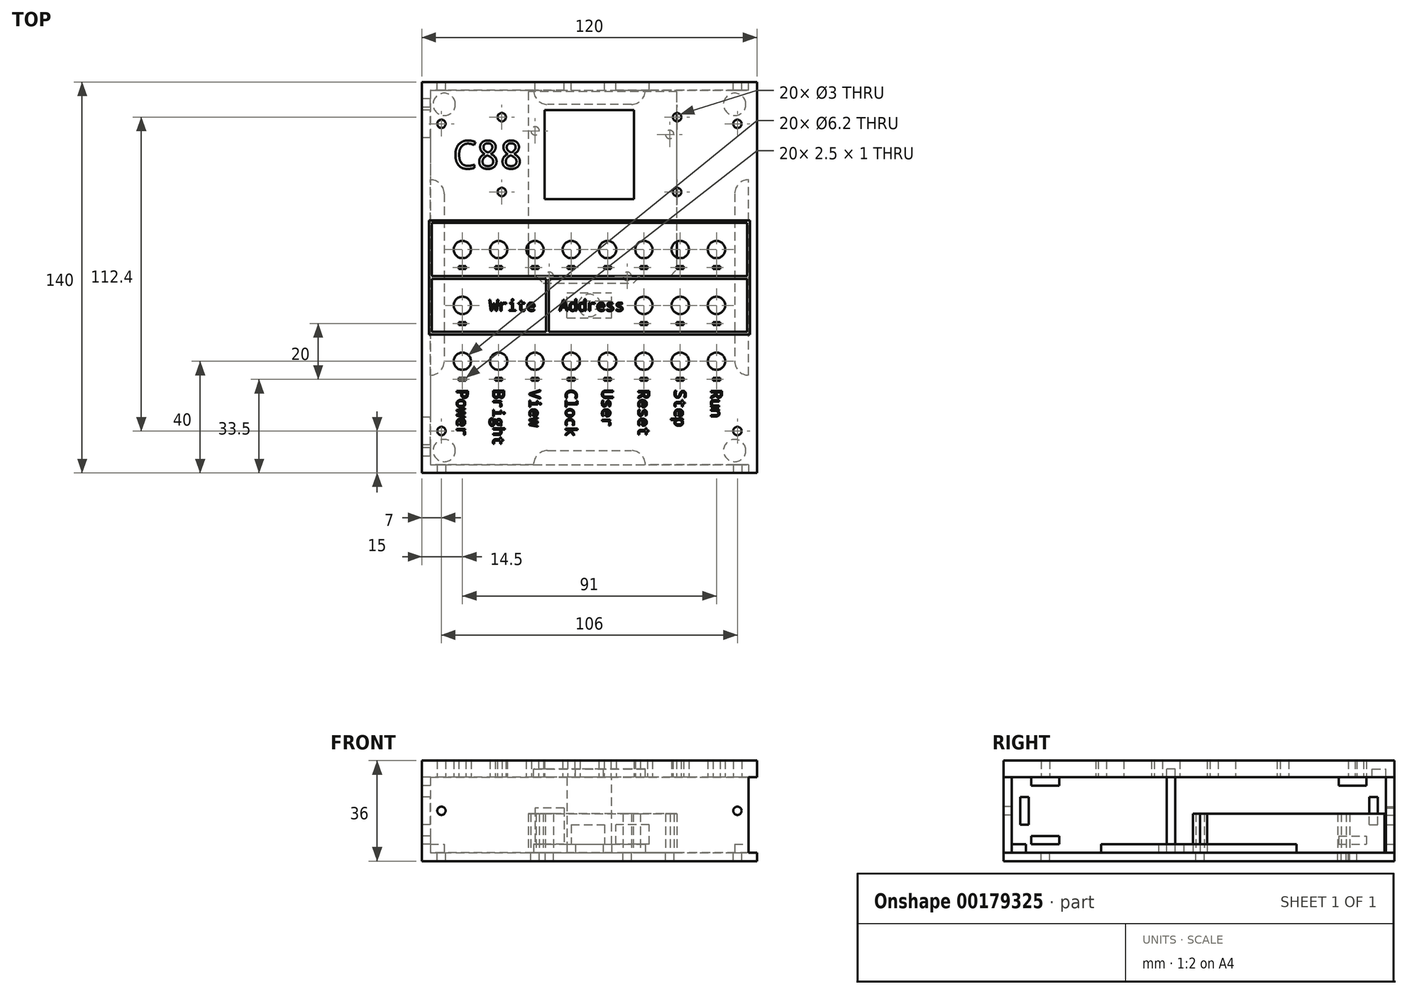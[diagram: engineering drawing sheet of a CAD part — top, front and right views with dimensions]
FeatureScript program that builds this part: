
annotation { "Feature Type Name" : "Feature", "Feature Type Description" : "" }
export const myFeature = defineFeature(function(context is Context, id is Id, definition is map)
    precondition{}
    {
        {
            assignVariable(context, id + "F0", {"name" : "thickness", "anyValue" : 3 * mm});
        }
        {
            var Q0;
            Q0=qCreatedBy(makeId("Top.planeOp"),FACE);
            var sketch = newSketch(context, id + "F1", { "sketchPlane" : qUnion([Q0])});
            skLineSegment(sketch, "E0.bottom", {"start": v(16, -16) * mm, "end": v(-16, -16) * mm});
            skLineSegment(sketch, "E0.top", {"start": v(16, 16) * mm, "end": v(-16, 16) * mm});
            skLineSegment(sketch, "E0.left", {"start": v(16, -16) * mm, "end": v(16, 16) * mm});
            skLineSegment(sketch, "E0.right", {"start": v(-16, -16) * mm, "end": v(-16, 16) * mm});
            skPoint(sketch, "E0.middle", {"position": v(0, 0) * mm});
            skCircle(sketch, "E1", {"center": v(31.4, 13.4) * mm, "radius": 1.5 * mm});
            skCircle(sketch, "E2", {"center": v(31.4, -13.4) * mm, "radius": 1.5 * mm});
            skLineSegment(sketch, "E3", {"start": v(-70.64, 0) * mm, "end": v(73.55, 0) * mm, "construction": true});
            skLineSegment(sketch, "E4.bottom", {"start": v(-60, 26) * mm, "end": v(60, 26) * mm});
            skLineSegment(sketch, "E4.top", {"start": v(-60, -114) * mm, "end": v(60, -114) * mm});
            skLineSegment(sketch, "E4.left", {"start": v(-60, 26) * mm, "end": v(-60, -114) * mm});
            skLineSegment(sketch, "E4.right", {"start": v(60, 26) * mm, "end": v(60, -114) * mm});
            skCircle(sketch, "E5", {"center": v(-31.4, -13.4) * mm, "radius": 1.5 * mm});
            skCircle(sketch, "E6", {"center": v(-31.4, 13.4) * mm, "radius": 1.5 * mm});
            skLineSegment(sketch, "E7", {"start": v(0, 36.27) * mm, "end": v(0, -161.9) * mm, "construction": true});
            skCircle(sketch, "E8", {"center": v(-45.5, -34) * mm, "radius": 3.1 * mm});
            skLineSegment(sketch, "E9.bottom", {"start": v(-44.25, -41) * mm, "end": v(-46.75, -41) * mm});
            skLineSegment(sketch, "E9.top", {"start": v(-44.25, -40) * mm, "end": v(-46.75, -40) * mm});
            skLineSegment(sketch, "E9.left", {"start": v(-44.25, -41) * mm, "end": v(-44.25, -40) * mm});
            skLineSegment(sketch, "E9.right", {"start": v(-46.75, -41) * mm, "end": v(-46.75, -40) * mm});
            skPoint(sketch, "E9.middle", {"position": v(-45.5, -40.5) * mm});
            skCircle(sketch, "E10.1.0.0", {"center": v(-32.5, -34) * mm, "radius": 3.1 * mm});
            skPoint(sketch, "E10.1.0.1", {"position": v(-32.5, -40.5) * mm});
            skLineSegment(sketch, "E10.1.0.2", {"start": v(-31.25, -41) * mm, "end": v(-31.25, -40) * mm});
            skLineSegment(sketch, "E10.1.0.3", {"start": v(-31.25, -41) * mm, "end": v(-33.75, -41) * mm});
            skLineSegment(sketch, "E10.1.0.4", {"start": v(-33.75, -41) * mm, "end": v(-33.75, -40) * mm});
            skLineSegment(sketch, "E10.1.0.5", {"start": v(-31.25, -40) * mm, "end": v(-33.75, -40) * mm});
            skCircle(sketch, "E10.2.0.0", {"center": v(-19.5, -34) * mm, "radius": 3.1 * mm});
            skPoint(sketch, "E10.2.0.1", {"position": v(-19.5, -40.5) * mm});
            skLineSegment(sketch, "E10.2.0.2", {"start": v(-18.25, -41) * mm, "end": v(-18.25, -40) * mm});
            skLineSegment(sketch, "E10.2.0.3", {"start": v(-18.25, -41) * mm, "end": v(-20.75, -41) * mm});
            skLineSegment(sketch, "E10.2.0.4", {"start": v(-20.75, -41) * mm, "end": v(-20.75, -40) * mm});
            skLineSegment(sketch, "E10.2.0.5", {"start": v(-18.25, -40) * mm, "end": v(-20.75, -40) * mm});
            skCircle(sketch, "E10.3.0.0", {"center": v(-6.5, -34) * mm, "radius": 3.1 * mm});
            skPoint(sketch, "E10.3.0.1", {"position": v(-6.5, -40.5) * mm});
            skLineSegment(sketch, "E10.3.0.2", {"start": v(-5.25, -41) * mm, "end": v(-5.25, -40) * mm});
            skLineSegment(sketch, "E10.3.0.3", {"start": v(-5.25, -41) * mm, "end": v(-7.75, -41) * mm});
            skLineSegment(sketch, "E10.3.0.4", {"start": v(-7.75, -41) * mm, "end": v(-7.75, -40) * mm});
            skLineSegment(sketch, "E10.3.0.5", {"start": v(-5.25, -40) * mm, "end": v(-7.75, -40) * mm});
            skCircle(sketch, "E10.4.0.0", {"center": v(6.5, -34) * mm, "radius": 3.1 * mm});
            skPoint(sketch, "E10.4.0.1", {"position": v(6.5, -40.5) * mm});
            skLineSegment(sketch, "E10.4.0.2", {"start": v(7.75, -41) * mm, "end": v(7.75, -40) * mm});
            skLineSegment(sketch, "E10.4.0.3", {"start": v(7.75, -41) * mm, "end": v(5.25, -41) * mm});
            skLineSegment(sketch, "E10.4.0.4", {"start": v(5.25, -41) * mm, "end": v(5.25, -40) * mm});
            skLineSegment(sketch, "E10.4.0.5", {"start": v(7.75, -40) * mm, "end": v(5.25, -40) * mm});
            skCircle(sketch, "E10.5.0.0", {"center": v(19.5, -34) * mm, "radius": 3.1 * mm});
            skPoint(sketch, "E10.5.0.1", {"position": v(19.5, -40.5) * mm});
            skLineSegment(sketch, "E10.5.0.2", {"start": v(20.75, -41) * mm, "end": v(20.75, -40) * mm});
            skLineSegment(sketch, "E10.5.0.3", {"start": v(20.75, -41) * mm, "end": v(18.25, -41) * mm});
            skLineSegment(sketch, "E10.5.0.4", {"start": v(18.25, -41) * mm, "end": v(18.25, -40) * mm});
            skLineSegment(sketch, "E10.5.0.5", {"start": v(20.75, -40) * mm, "end": v(18.25, -40) * mm});
            skCircle(sketch, "E10.6.0.0", {"center": v(32.5, -34) * mm, "radius": 3.1 * mm});
            skPoint(sketch, "E10.6.0.1", {"position": v(32.5, -40.5) * mm});
            skLineSegment(sketch, "E10.6.0.2", {"start": v(33.75, -41) * mm, "end": v(33.75, -40) * mm});
            skLineSegment(sketch, "E10.6.0.3", {"start": v(33.75, -41) * mm, "end": v(31.25, -41) * mm});
            skLineSegment(sketch, "E10.6.0.4", {"start": v(31.25, -41) * mm, "end": v(31.25, -40) * mm});
            skLineSegment(sketch, "E10.6.0.5", {"start": v(33.75, -40) * mm, "end": v(31.25, -40) * mm});
            skCircle(sketch, "E10.7.0.0", {"center": v(45.5, -34) * mm, "radius": 3.1 * mm});
            skPoint(sketch, "E10.7.0.1", {"position": v(45.5, -40.5) * mm});
            skLineSegment(sketch, "E10.7.0.2", {"start": v(46.75, -41) * mm, "end": v(46.75, -40) * mm});
            skLineSegment(sketch, "E10.7.0.3", {"start": v(46.75, -41) * mm, "end": v(44.25, -41) * mm});
            skLineSegment(sketch, "E10.7.0.4", {"start": v(44.25, -41) * mm, "end": v(44.25, -40) * mm});
            skLineSegment(sketch, "E10.7.0.5", {"start": v(46.75, -40) * mm, "end": v(44.25, -40) * mm});
            skLineSegment(sketch, "E10.direction1", {"start": v(-46.75, -41) * mm, "end": v(-33.75, -41) * mm, "construction": true});
            skCircle(sketch, "E11.1.0.0", {"center": v(32.5, -54) * mm, "radius": 3.1 * mm});
            skPoint(sketch, "E11.1.0.1", {"position": v(32.5, -60.5) * mm});
            skPoint(sketch, "E11.1.0.2", {"position": v(19.5, -60.5) * mm});
            skCircle(sketch, "E11.1.0.3", {"center": v(45.5, -54) * mm, "radius": 3.1 * mm});
            skCircle(sketch, "E11.1.0.4", {"center": v(19.5, -54) * mm, "radius": 3.1 * mm});
            skPoint(sketch, "E11.1.0.5", {"position": v(45.5, -60.5) * mm});
            skLineSegment(sketch, "E11.1.0.6", {"start": v(33.75, -61) * mm, "end": v(31.25, -61) * mm});
            skLineSegment(sketch, "E11.1.0.7", {"start": v(46.75, -60) * mm, "end": v(44.25, -60) * mm});
            skLineSegment(sketch, "E11.1.0.8", {"start": v(46.75, -61) * mm, "end": v(46.75, -60) * mm});
            skLineSegment(sketch, "E11.1.0.9", {"start": v(20.75, -61) * mm, "end": v(18.25, -61) * mm});
            skLineSegment(sketch, "E11.1.0.10", {"start": v(33.75, -60) * mm, "end": v(31.25, -60) * mm});
            skLineSegment(sketch, "E11.1.0.11", {"start": v(44.25, -61) * mm, "end": v(44.25, -60) * mm});
            skLineSegment(sketch, "E11.1.0.12", {"start": v(20.75, -60) * mm, "end": v(18.25, -60) * mm});
            skLineSegment(sketch, "E11.1.0.13", {"start": v(46.75, -61) * mm, "end": v(44.25, -61) * mm});
            skLineSegment(sketch, "E11.1.0.14", {"start": v(31.25, -61) * mm, "end": v(31.25, -60) * mm});
            skLineSegment(sketch, "E11.1.0.15", {"start": v(20.75, -61) * mm, "end": v(20.75, -60) * mm});
            skLineSegment(sketch, "E11.1.0.16", {"start": v(33.75, -61) * mm, "end": v(33.75, -60) * mm});
            skLineSegment(sketch, "E11.1.0.17", {"start": v(18.25, -61) * mm, "end": v(18.25, -60) * mm});
            skLineSegment(sketch, "E11.direction1", {"start": v(18.25, -41) * mm, "end": v(18.25, -61) * mm, "construction": true});
            skPoint(sketch, "E12.1.0.0", {"position": v(-45.5, -60.5) * mm});
            skCircle(sketch, "E12.1.0.1", {"center": v(-45.5, -54) * mm, "radius": 3.1 * mm});
            skLineSegment(sketch, "E12.1.0.2", {"start": v(-44.25, -61) * mm, "end": v(-46.75, -61) * mm});
            skLineSegment(sketch, "E12.1.0.3", {"start": v(-44.25, -60) * mm, "end": v(-46.75, -60) * mm});
            skLineSegment(sketch, "E12.1.0.4", {"start": v(-44.25, -61) * mm, "end": v(-44.25, -60) * mm});
            skLineSegment(sketch, "E12.1.0.5", {"start": v(-46.75, -61) * mm, "end": v(-46.75, -60) * mm});
            skLineSegment(sketch, "E12.direction1", {"start": v(-46.75, -41) * mm, "end": v(-46.75, -61) * mm, "construction": true});
            skPoint(sketch, "E13.0.2.0", {"position": v(-45.5, -80.5) * mm});
            skCircle(sketch, "E13.1.2.0", {"center": v(-45.5, -74) * mm, "radius": 3.1 * mm});
            skLineSegment(sketch, "E13.3.2.0", {"start": v(-44.25, -81) * mm, "end": v(-46.75, -81) * mm});
            skLineSegment(sketch, "E13.6.2.0", {"start": v(-44.25, -80) * mm, "end": v(-46.75, -80) * mm});
            skLineSegment(sketch, "E13.9.2.0", {"start": v(-44.25, -81) * mm, "end": v(-44.25, -80) * mm});
            skLineSegment(sketch, "E13.12.2.0", {"start": v(-46.75, -81) * mm, "end": v(-46.75, -80) * mm});
            skLineSegment(sketch, "E14.1.0.0", {"start": v(-31.25, -80) * mm, "end": v(-33.75, -80) * mm});
            skLineSegment(sketch, "E14.1.0.1", {"start": v(-31.25, -81) * mm, "end": v(-33.75, -81) * mm});
            skLineSegment(sketch, "E14.1.0.2", {"start": v(-31.25, -81) * mm, "end": v(-31.25, -80) * mm});
            skLineSegment(sketch, "E14.1.0.3", {"start": v(-33.75, -81) * mm, "end": v(-33.75, -80) * mm});
            skPoint(sketch, "E14.1.0.4", {"position": v(-32.5, -80.5) * mm});
            skCircle(sketch, "E14.1.0.5", {"center": v(-32.5, -74) * mm, "radius": 3.1 * mm});
            skLineSegment(sketch, "E14.2.0.0", {"start": v(-18.25, -80) * mm, "end": v(-20.75, -80) * mm});
            skLineSegment(sketch, "E14.2.0.1", {"start": v(-18.25, -81) * mm, "end": v(-20.75, -81) * mm});
            skLineSegment(sketch, "E14.2.0.2", {"start": v(-18.25, -81) * mm, "end": v(-18.25, -80) * mm});
            skLineSegment(sketch, "E14.2.0.3", {"start": v(-20.75, -81) * mm, "end": v(-20.75, -80) * mm});
            skPoint(sketch, "E14.2.0.4", {"position": v(-19.5, -80.5) * mm});
            skCircle(sketch, "E14.2.0.5", {"center": v(-19.5, -74) * mm, "radius": 3.1 * mm});
            skLineSegment(sketch, "E14.3.0.0", {"start": v(-5.25, -80) * mm, "end": v(-7.75, -80) * mm});
            skLineSegment(sketch, "E14.3.0.1", {"start": v(-5.25, -81) * mm, "end": v(-7.75, -81) * mm});
            skLineSegment(sketch, "E14.3.0.2", {"start": v(-5.25, -81) * mm, "end": v(-5.25, -80) * mm});
            skLineSegment(sketch, "E14.3.0.3", {"start": v(-7.75, -81) * mm, "end": v(-7.75, -80) * mm});
            skPoint(sketch, "E14.3.0.4", {"position": v(-6.5, -80.5) * mm});
            skCircle(sketch, "E14.3.0.5", {"center": v(-6.5, -74) * mm, "radius": 3.1 * mm});
            skLineSegment(sketch, "E14.4.0.0", {"start": v(7.75, -80) * mm, "end": v(5.25, -80) * mm});
            skLineSegment(sketch, "E14.4.0.1", {"start": v(7.75, -81) * mm, "end": v(5.25, -81) * mm});
            skLineSegment(sketch, "E14.4.0.2", {"start": v(7.75, -81) * mm, "end": v(7.75, -80) * mm});
            skLineSegment(sketch, "E14.4.0.3", {"start": v(5.25, -81) * mm, "end": v(5.25, -80) * mm});
            skPoint(sketch, "E14.4.0.4", {"position": v(6.5, -80.5) * mm});
            skCircle(sketch, "E14.4.0.5", {"center": v(6.5, -74) * mm, "radius": 3.1 * mm});
            skLineSegment(sketch, "E14.5.0.0", {"start": v(20.75, -80) * mm, "end": v(18.25, -80) * mm});
            skLineSegment(sketch, "E14.5.0.1", {"start": v(20.75, -81) * mm, "end": v(18.25, -81) * mm});
            skLineSegment(sketch, "E14.5.0.2", {"start": v(20.75, -81) * mm, "end": v(20.75, -80) * mm});
            skLineSegment(sketch, "E14.5.0.3", {"start": v(18.25, -81) * mm, "end": v(18.25, -80) * mm});
            skPoint(sketch, "E14.5.0.4", {"position": v(19.5, -80.5) * mm});
            skCircle(sketch, "E14.5.0.5", {"center": v(19.5, -74) * mm, "radius": 3.1 * mm});
            skLineSegment(sketch, "E14.6.0.0", {"start": v(33.75, -80) * mm, "end": v(31.25, -80) * mm});
            skLineSegment(sketch, "E14.6.0.1", {"start": v(33.75, -81) * mm, "end": v(31.25, -81) * mm});
            skLineSegment(sketch, "E14.6.0.2", {"start": v(33.75, -81) * mm, "end": v(33.75, -80) * mm});
            skLineSegment(sketch, "E14.6.0.3", {"start": v(31.25, -81) * mm, "end": v(31.25, -80) * mm});
            skPoint(sketch, "E14.6.0.4", {"position": v(32.5, -80.5) * mm});
            skCircle(sketch, "E14.6.0.5", {"center": v(32.5, -74) * mm, "radius": 3.1 * mm});
            skLineSegment(sketch, "E14.7.0.0", {"start": v(46.75, -80) * mm, "end": v(44.25, -80) * mm});
            skLineSegment(sketch, "E14.7.0.1", {"start": v(46.75, -81) * mm, "end": v(44.25, -81) * mm});
            skLineSegment(sketch, "E14.7.0.2", {"start": v(46.75, -81) * mm, "end": v(46.75, -80) * mm});
            skLineSegment(sketch, "E14.7.0.3", {"start": v(44.25, -81) * mm, "end": v(44.25, -80) * mm});
            skPoint(sketch, "E14.7.0.4", {"position": v(45.5, -80.5) * mm});
            skCircle(sketch, "E14.7.0.5", {"center": v(45.5, -74) * mm, "radius": 3.1 * mm});
            skLineSegment(sketch, "E14.direction1", {"start": v(-46.75, -81) * mm, "end": v(-33.75, -81) * mm, "construction": true});
            skCircle(sketch, "E15", {"center": v(53, -99) * mm, "radius": 1.5 * mm});
            skCircle(sketch, "E16", {"center": v(-53, -99) * mm, "radius": 1.5 * mm});
            skCircle(sketch, "E17", {"center": v(-53, 11) * mm, "radius": 1.5 * mm});
            skCircle(sketch, "E18", {"center": v(53, 11) * mm, "radius": 1.5 * mm});
            skSolve(sketch);
        }
        {
            var Q0;
            Q0=makeQuery(id+"F1.imprint","IMPRINT",FACE,{"disambiguationData":[TD([[makeQuery(id+"F1.imprint","IMPRINT",EDGE,{"derivedFrom":sQuery(id+"F1.wireOp",EDGE,"E0.bottom")}),1.0]])]});
            extrude(context, id + "F2", {"entities" : qUnion([Q0]), "depth" : getVariable(context, 'thickness')});
        }
        {
            var Q0;
            Q0=makeQuery(id+"F2.opExtrude","CAP_FACE",FACE,{"disambiguationData":[OSD([sQuery(id+"F1.wireOp",EDGE,"E0.bottom"),sQuery(id+"F1.wireOp",EDGE,"E0.top"),sQuery(id+"F1.wireOp",EDGE,"E0.left"),sQuery(id+"F1.wireOp",EDGE,"E0.right"),sQuery(id+"F1.wireOp",EDGE,"E1"),sQuery(id+"F1.wireOp",EDGE,"E2"),sQuery(id+"F1.wireOp",EDGE,"E4.bottom"),sQuery(id+"F1.wireOp",EDGE,"E4.top"),sQuery(id+"F1.wireOp",EDGE,"E4.left"),sQuery(id+"F1.wireOp",EDGE,"E4.right"),sQuery(id+"F1.wireOp",EDGE,"E5"),sQuery(id+"F1.wireOp",EDGE,"E6"),sQuery(id+"F1.wireOp",EDGE,"E8"),sQuery(id+"F1.wireOp",EDGE,"E9.bottom"),sQuery(id+"F1.wireOp",EDGE,"E9.top"),sQuery(id+"F1.wireOp",EDGE,"E9.left"),sQuery(id+"F1.wireOp",EDGE,"E9.right"),sQuery(id+"F1.wireOp",EDGE,"E10.1.0.0"),sQuery(id+"F1.wireOp",EDGE,"E10.1.0.2"),sQuery(id+"F1.wireOp",EDGE,"E10.1.0.3"),sQuery(id+"F1.wireOp",EDGE,"E10.1.0.4"),sQuery(id+"F1.wireOp",EDGE,"E10.1.0.5"),sQuery(id+"F1.wireOp",EDGE,"E10.2.0.0"),sQuery(id+"F1.wireOp",EDGE,"E10.2.0.2"),sQuery(id+"F1.wireOp",EDGE,"E10.2.0.3"),sQuery(id+"F1.wireOp",EDGE,"E10.2.0.4"),sQuery(id+"F1.wireOp",EDGE,"E10.2.0.5"),sQuery(id+"F1.wireOp",EDGE,"E10.3.0.0"),sQuery(id+"F1.wireOp",EDGE,"E10.3.0.2"),sQuery(id+"F1.wireOp",EDGE,"E10.3.0.3"),sQuery(id+"F1.wireOp",EDGE,"E10.3.0.4"),sQuery(id+"F1.wireOp",EDGE,"E10.3.0.5"),sQuery(id+"F1.wireOp",EDGE,"E10.4.0.0"),sQuery(id+"F1.wireOp",EDGE,"E10.4.0.2"),sQuery(id+"F1.wireOp",EDGE,"E10.4.0.3"),sQuery(id+"F1.wireOp",EDGE,"E10.4.0.4"),sQuery(id+"F1.wireOp",EDGE,"E10.4.0.5"),sQuery(id+"F1.wireOp",EDGE,"E10.5.0.0"),sQuery(id+"F1.wireOp",EDGE,"E10.5.0.2"),sQuery(id+"F1.wireOp",EDGE,"E10.5.0.3"),sQuery(id+"F1.wireOp",EDGE,"E10.5.0.4"),sQuery(id+"F1.wireOp",EDGE,"E10.5.0.5"),sQuery(id+"F1.wireOp",EDGE,"E10.6.0.0"),sQuery(id+"F1.wireOp",EDGE,"E10.6.0.2"),sQuery(id+"F1.wireOp",EDGE,"E10.6.0.3"),sQuery(id+"F1.wireOp",EDGE,"E10.6.0.4"),sQuery(id+"F1.wireOp",EDGE,"E10.6.0.5"),sQuery(id+"F1.wireOp",EDGE,"E10.7.0.0"),sQuery(id+"F1.wireOp",EDGE,"E10.7.0.2"),sQuery(id+"F1.wireOp",EDGE,"E10.7.0.3"),sQuery(id+"F1.wireOp",EDGE,"E10.7.0.4"),sQuery(id+"F1.wireOp",EDGE,"E10.7.0.5"),sQuery(id+"F1.wireOp",EDGE,"E11.1.0.0"),sQuery(id+"F1.wireOp",EDGE,"E11.1.0.3"),sQuery(id+"F1.wireOp",EDGE,"E11.1.0.4"),sQuery(id+"F1.wireOp",EDGE,"E11.1.0.6"),sQuery(id+"F1.wireOp",EDGE,"E11.1.0.7"),sQuery(id+"F1.wireOp",EDGE,"E11.1.0.8"),sQuery(id+"F1.wireOp",EDGE,"E11.1.0.9"),sQuery(id+"F1.wireOp",EDGE,"E11.1.0.10"),sQuery(id+"F1.wireOp",EDGE,"E11.1.0.11"),sQuery(id+"F1.wireOp",EDGE,"E11.1.0.12"),sQuery(id+"F1.wireOp",EDGE,"E11.1.0.13"),sQuery(id+"F1.wireOp",EDGE,"E11.1.0.14"),sQuery(id+"F1.wireOp",EDGE,"E11.1.0.15"),sQuery(id+"F1.wireOp",EDGE,"E11.1.0.16"),sQuery(id+"F1.wireOp",EDGE,"E11.1.0.17"),sQuery(id+"F1.wireOp",EDGE,"E12.1.0.1"),sQuery(id+"F1.wireOp",EDGE,"E12.1.0.2"),sQuery(id+"F1.wireOp",EDGE,"E12.1.0.3"),sQuery(id+"F1.wireOp",EDGE,"E12.1.0.4"),sQuery(id+"F1.wireOp",EDGE,"E12.1.0.5"),sQuery(id+"F1.wireOp",EDGE,"E13.1.2.0"),sQuery(id+"F1.wireOp",EDGE,"E13.3.2.0"),sQuery(id+"F1.wireOp",EDGE,"E13.6.2.0"),sQuery(id+"F1.wireOp",EDGE,"E13.9.2.0"),sQuery(id+"F1.wireOp",EDGE,"E13.12.2.0"),sQuery(id+"F1.wireOp",EDGE,"E14.1.0.0"),sQuery(id+"F1.wireOp",EDGE,"E14.1.0.1"),sQuery(id+"F1.wireOp",EDGE,"E14.1.0.2"),sQuery(id+"F1.wireOp",EDGE,"E14.1.0.3"),sQuery(id+"F1.wireOp",EDGE,"E14.1.0.5"),sQuery(id+"F1.wireOp",EDGE,"E14.2.0.0"),sQuery(id+"F1.wireOp",EDGE,"E14.2.0.1"),sQuery(id+"F1.wireOp",EDGE,"E14.2.0.2"),sQuery(id+"F1.wireOp",EDGE,"E14.2.0.3"),sQuery(id+"F1.wireOp",EDGE,"E14.2.0.5"),sQuery(id+"F1.wireOp",EDGE,"E14.3.0.0"),sQuery(id+"F1.wireOp",EDGE,"E14.3.0.1"),sQuery(id+"F1.wireOp",EDGE,"E14.3.0.2"),sQuery(id+"F1.wireOp",EDGE,"E14.3.0.3"),sQuery(id+"F1.wireOp",EDGE,"E14.3.0.5"),sQuery(id+"F1.wireOp",EDGE,"E14.4.0.0"),sQuery(id+"F1.wireOp",EDGE,"E14.4.0.1"),sQuery(id+"F1.wireOp",EDGE,"E14.4.0.2"),sQuery(id+"F1.wireOp",EDGE,"E14.4.0.3"),sQuery(id+"F1.wireOp",EDGE,"E14.4.0.5"),sQuery(id+"F1.wireOp",EDGE,"E14.5.0.0"),sQuery(id+"F1.wireOp",EDGE,"E14.5.0.1"),sQuery(id+"F1.wireOp",EDGE,"E14.5.0.2"),sQuery(id+"F1.wireOp",EDGE,"E14.5.0.3"),sQuery(id+"F1.wireOp",EDGE,"E14.5.0.5"),sQuery(id+"F1.wireOp",EDGE,"E14.6.0.0"),sQuery(id+"F1.wireOp",EDGE,"E14.6.0.1"),sQuery(id+"F1.wireOp",EDGE,"E14.6.0.2"),sQuery(id+"F1.wireOp",EDGE,"E14.6.0.3"),sQuery(id+"F1.wireOp",EDGE,"E14.6.0.5"),sQuery(id+"F1.wireOp",EDGE,"E14.7.0.0"),sQuery(id+"F1.wireOp",EDGE,"E14.7.0.1"),sQuery(id+"F1.wireOp",EDGE,"E14.7.0.2"),sQuery(id+"F1.wireOp",EDGE,"E14.7.0.3"),sQuery(id+"F1.wireOp",EDGE,"E14.7.0.5")])],"isStart":false});
            var sketch = newSketch(context, id + "F3", { "sketchPlane" : qUnion([Q0])});
            skText(sketch, "E19", { "text": "C88", "fontName": "DroidSansMono.ttf"});
            skLineSegment(sketch, "E20", {"start": v(-64.19, 0) * mm, "end": v(81.6, 0) * mm, "construction": true});
            skText(sketch, "E21", { "text": "Run", "fontName": "DroidSansMono.ttf"});
            skLineSegment(sketch, "E22.top", {"start": v(-57.5, -64.5) * mm, "end": v(-18.42, -64.5) * mm});
            skLineSegment(sketch, "E22.left", {"start": v(-57.5, -47.87) * mm, "end": v(-57.5, -64.5) * mm});
            skLineSegment(sketch, "E23.top", {"start": v(-18.42, -64.5) * mm, "end": v(57.5, -64.5) * mm});
            skLineSegment(sketch, "E23.right", {"start": v(57.5, -51.64) * mm, "end": v(57.5, -64.5) * mm});
            skLineSegment(sketch, "E24.bottom", {"start": v(-56.5, -44.5) * mm, "end": v(-15.58, -44.5) * mm});
            skLineSegment(sketch, "E24.top", {"start": v(-56.5, -63.5) * mm, "end": v(-15.58, -63.5) * mm});
            skLineSegment(sketch, "E24.left", {"start": v(-56.5, -44.5) * mm, "end": v(-56.5, -63.5) * mm});
            skLineSegment(sketch, "E24.right", {"start": v(-15.58, -44.5) * mm, "end": v(-15.58, -63.5) * mm});
            skLineSegment(sketch, "E25.bottom", {"start": v(-14.58, -44.5) * mm, "end": v(56.5, -44.5) * mm});
            skLineSegment(sketch, "E25.top", {"start": v(-14.58, -63.5) * mm, "end": v(56.5, -63.5) * mm});
            skLineSegment(sketch, "E25.left", {"start": v(-14.58, -44.5) * mm, "end": v(-14.58, -63.5) * mm});
            skLineSegment(sketch, "E25.right", {"start": v(56.5, -44.5) * mm, "end": v(56.5, -63.5) * mm});
            skLineSegment(sketch, "E26.top", {"start": v(57.5, -23.5) * mm, "end": v(-57.5, -23.5) * mm});
            skLineSegment(sketch, "E26.left", {"start": v(57.5, -51.64) * mm, "end": v(57.5, -23.5) * mm});
            skLineSegment(sketch, "E26.right", {"start": v(-57.5, -47.87) * mm, "end": v(-57.5, -23.5) * mm});
            skLineSegment(sketch, "E27.bottom", {"start": v(-56.5, -24.5) * mm, "end": v(56.5, -24.5) * mm});
            skLineSegment(sketch, "E27.top", {"start": v(-56.5, -43.5) * mm, "end": v(56.5, -43.5) * mm});
            skLineSegment(sketch, "E27.left", {"start": v(-56.5, -24.5) * mm, "end": v(-56.5, -43.5) * mm});
            skLineSegment(sketch, "E27.right", {"start": v(56.5, -24.5) * mm, "end": v(56.5, -43.5) * mm});
            skLineSegment(sketch, "E28", {"start": v(0, 42.83) * mm, "end": v(0, -126.8) * mm, "construction": true});
            skText(sketch, "E29", { "text": "Write", "fontName": "DroidSansMono.ttf"});
            skText(sketch, "E30", { "text": "Address\n", "fontName": "DroidSansMono.ttf"});
            skLineSegment(sketch, "E31", {"start": v(-45.5, -54) * mm, "end": v(45.5, -54) * mm, "construction": true});
            skLineSegment(sketch, "E32", {"start": v(-45.5, -34) * mm, "end": v(45.5, -34) * mm, "construction": true});
            skLineSegment(sketch, "E33", {"start": v(-45.5, -74) * mm, "end": v(45.5, -74) * mm, "construction": true});
            skLineSegment(sketch, "E34", {"start": v(45.5, -34) * mm, "end": v(45.5, -74) * mm, "construction": true});
            skLineSegment(sketch, "E35", {"start": v(32.5, -34) * mm, "end": v(32.5, -74) * mm, "construction": true});
            skLineSegment(sketch, "E36", {"start": v(19.5, -34) * mm, "end": v(19.5, -74) * mm, "construction": true});
            skLineSegment(sketch, "E37", {"start": v(6.5, -34) * mm, "end": v(6.5, -74) * mm, "construction": true});
            skLineSegment(sketch, "E38", {"start": v(-6.5, -34) * mm, "end": v(-6.5, -74) * mm, "construction": true});
            skLineSegment(sketch, "E39", {"start": v(-19.5, -34) * mm, "end": v(-19.5, -74) * mm, "construction": true});
            skLineSegment(sketch, "E40", {"start": v(-32.5, -34) * mm, "end": v(-32.5, -74) * mm, "construction": true});
            skLineSegment(sketch, "E41", {"start": v(-45.5, -34) * mm, "end": v(-45.5, -74) * mm, "construction": true});
            skText(sketch, "E42", { "text": "Step", "fontName": "DroidSansMono.ttf"});
            skText(sketch, "E43", { "text": "Reset", "fontName": "DroidSansMono.ttf"});
            skText(sketch, "E44", { "text": "User", "fontName": "DroidSansMono.ttf"});
            skText(sketch, "E45", { "text": "Power", "fontName": "DroidSansMono.ttf"});
            skText(sketch, "E46", { "text": "Bright", "fontName": "DroidSansMono.ttf"});
            skText(sketch, "E47", { "text": "Clock", "fontName": "DroidSansMono.ttf"});
            skText(sketch, "E48", { "text": "View", "fontName": "DroidSansMono.ttf"});
            const initialGuessF3  = {"E19": [-0.04886, -0.005, 1, 0, 0.01], "E21": [0.0435, -0.08417, 0, -1, 0.004], "E29": [-0.03593, -0.056, 1, 0, 0.004], "E30": [-0.0109, -0.056, 1, 0, 0.004], "E42": [0.0305, -0.08417, 0, -1, 0.004], "E43": [0.0175, -0.08417, 0, -1, 0.004], "E44": [0.0045, -0.08417, 0, -1, 0.004], "E45": [-0.0475, -0.08417, 0, -1, 0.004], "E46": [-0.0345, -0.08417, 0, -1, 0.004], "E47": [-0.0085, -0.08417, 0, -1, 0.004], "E48": [-0.0215, -0.08417, 0, -1, 0.004]};
            skSetInitialGuess(sketch, initialGuessF3);
            skSolve(sketch);
        }
        {
            var Q0;
            Q0 = qSketchRegion(id + "F3", true);
            extrude(context, id + "F4", {"entities" : qUnion([Q0]), "operationType" : NewBodyOperationType.REMOVE, "oppositeDirection" : true, "depth" : 0.1 * mm});
        }
        {
            var Q0;
            Q0=makeQuery(id+"F3.imprint","IMPRINT",FACE,{"disambiguationData":[TD([[makeQuery(id+"F3.imprint","IMPRINT",EDGE,{"derivedFrom":sQuery(id+"F3.wireOp",EDGE,"E29.sketch_text.stroke-0")}),-1.0]])]});
            var Q1;
            Q1=makeQuery(id+"F3.imprint","IMPRINT",FACE,{"disambiguationData":[TD([[makeQuery(id+"F3.imprint","IMPRINT",EDGE,{"derivedFrom":sQuery(id+"F3.wireOp",EDGE,"E29.sketch_text.stroke-20")}),-1.0]])]});
            var Q2;
            Q2=makeQuery(id+"F3.imprint","IMPRINT",FACE,{"disambiguationData":[TD([[makeQuery(id+"F3.imprint","IMPRINT",EDGE,{"derivedFrom":sQuery(id+"F3.wireOp",EDGE,"E29.sketch_text.stroke-38")}),-1.0]])]});
            var Q3;
            Q3=makeQuery(id+"F3.imprint","IMPRINT",FACE,{"disambiguationData":[TD([[makeQuery(id+"F3.imprint","IMPRINT",EDGE,{"derivedFrom":sQuery(id+"F3.wireOp",EDGE,"E29.sketch_text.stroke-33")}),-1.0]])]});
            var Q4;
            Q4=makeQuery(id+"F3.imprint","IMPRINT",FACE,{"disambiguationData":[TD([[makeQuery(id+"F3.imprint","IMPRINT",EDGE,{"derivedFrom":sQuery(id+"F3.wireOp",EDGE,"E29.sketch_text.stroke-48")}),-1.0]])]});
            var Q5;
            Q5=makeQuery(id+"F3.imprint","IMPRINT",FACE,{"disambiguationData":[TD([[makeQuery(id+"F3.imprint","IMPRINT",EDGE,{"derivedFrom":sQuery(id+"F3.wireOp",EDGE,"E29.sketch_text.stroke-64")}),-1.0]])]});
            extrude(context, id + "F5", {"entities" : qUnion([Q0, Q1, Q2, Q3, Q4, Q5]), "operationType" : NewBodyOperationType.REMOVE, "oppositeDirection" : true, "depth" : 0.1 * mm});
        }
        {
            var Q0;
            Q0=makeQuery(id+"F3.imprint","IMPRINT",FACE,{"disambiguationData":[TD([[makeQuery(id+"F3.imprint","IMPRINT",EDGE,{"derivedFrom":sQuery(id+"F3.wireOp",EDGE,"E30.sketch_text.stroke-0")}),-1.0]])]});
            var Q1;
            Q1=makeQuery(id+"F3.imprint","IMPRINT",FACE,{"disambiguationData":[TD([[makeQuery(id+"F3.imprint","IMPRINT",EDGE,{"derivedFrom":sQuery(id+"F3.wireOp",EDGE,"E30.sketch_text.stroke-13")}),-1.0]])]});
            var Q2;
            Q2=makeQuery(id+"F3.imprint","IMPRINT",FACE,{"disambiguationData":[TD([[makeQuery(id+"F3.imprint","IMPRINT",EDGE,{"derivedFrom":sQuery(id+"F3.wireOp",EDGE,"E30.sketch_text.stroke-34")}),-1.0]])]});
            var Q3;
            Q3=makeQuery(id+"F3.imprint","IMPRINT",FACE,{"disambiguationData":[TD([[makeQuery(id+"F3.imprint","IMPRINT",EDGE,{"derivedFrom":sQuery(id+"F3.wireOp",EDGE,"E30.sketch_text.stroke-55")}),-1.0]])]});
            var Q4;
            Q4=makeQuery(id+"F3.imprint","IMPRINT",FACE,{"disambiguationData":[TD([[makeQuery(id+"F3.imprint","IMPRINT",EDGE,{"derivedFrom":sQuery(id+"F3.wireOp",EDGE,"E30.sketch_text.stroke-68")}),-1.0]])]});
            var Q5;
            Q5=makeQuery(id+"F3.imprint","IMPRINT",FACE,{"disambiguationData":[TD([[makeQuery(id+"F3.imprint","IMPRINT",EDGE,{"derivedFrom":sQuery(id+"F3.wireOp",EDGE,"E30.sketch_text.stroke-83")}),-1.0]])]});
            var Q6;
            Q6=makeQuery(id+"F3.imprint","IMPRINT",FACE,{"disambiguationData":[TD([[makeQuery(id+"F3.imprint","IMPRINT",EDGE,{"derivedFrom":sQuery(id+"F3.wireOp",EDGE,"E30.sketch_text.stroke-103")}),-1.0]])]});
            extrude(context, id + "F6", {"entities" : qUnion([Q0, Q1, Q2, Q3, Q4, Q5, Q6]), "operationType" : NewBodyOperationType.REMOVE, "oppositeDirection" : true, "depth" : 0.1 * mm});
        }
        {
            var Q0;
            Q0=makeQuery(id+"F2.opExtrude","SWEPT_FACE",FACE,{"disambiguationData":[OSD([sQuery(id+"F1.wireOp",EDGE,"E4.left")])]});
            var sketch = newSketch(context, id + "F7", { "sketchPlane" : qUnion([Q0])});
            skLineSegment(sketch, "E49.bottom", {"start": v(-26, 0) * mm, "end": v(114, 0) * mm});
            skLineSegment(sketch, "E49.top", {"start": v(-26, -30) * mm, "end": v(114, -30) * mm});
            skLineSegment(sketch, "E49.left", {"start": v(-26, 0) * mm, "end": v(-26, -30) * mm});
            skLineSegment(sketch, "E49.right", {"start": v(114, 0) * mm, "end": v(114, -30) * mm});
            skLineSegment(sketch, "E50.bottom", {"start": v(-6, -3) * mm, "end": v(-16, -3) * mm});
            skLineSegment(sketch, "E50.top", {"start": v(-6, -6) * mm, "end": v(-16, -6) * mm});
            skLineSegment(sketch, "E50.left", {"start": v(-6, -3) * mm, "end": v(-6, -6) * mm});
            skLineSegment(sketch, "E50.right", {"start": v(-16, -3) * mm, "end": v(-16, -6) * mm});
            skPoint(sketch, "E50.middle", {"position": v(-11, -4.5) * mm});
            skLineSegment(sketch, "E51.0.1.0", {"start": v(-6, -27) * mm, "end": v(-16, -27) * mm});
            skLineSegment(sketch, "E51.0.1.1", {"start": v(-6, -24) * mm, "end": v(-16, -24) * mm});
            skPoint(sketch, "E51.0.1.2", {"position": v(-11, -25.5) * mm});
            skLineSegment(sketch, "E51.0.1.3", {"start": v(-6, -24) * mm, "end": v(-6, -27) * mm});
            skLineSegment(sketch, "E51.0.1.4", {"start": v(-16, -24) * mm, "end": v(-16, -27) * mm});
            skLineSegment(sketch, "E51.1.0.0", {"start": v(104, -6) * mm, "end": v(94, -6) * mm});
            skLineSegment(sketch, "E51.1.0.1", {"start": v(104, -3) * mm, "end": v(94, -3) * mm});
            skPoint(sketch, "E51.1.0.2", {"position": v(99, -4.5) * mm});
            skLineSegment(sketch, "E51.1.0.3", {"start": v(104, -3) * mm, "end": v(104, -6) * mm});
            skLineSegment(sketch, "E51.1.0.4", {"start": v(94, -3) * mm, "end": v(94, -6) * mm});
            skLineSegment(sketch, "E51.1.1.0", {"start": v(104, -27) * mm, "end": v(94, -27) * mm});
            skLineSegment(sketch, "E51.1.1.1", {"start": v(104, -24) * mm, "end": v(94, -24) * mm});
            skPoint(sketch, "E51.1.1.2", {"position": v(99, -25.5) * mm});
            skLineSegment(sketch, "E51.1.1.3", {"start": v(104, -24) * mm, "end": v(104, -27) * mm});
            skLineSegment(sketch, "E51.1.1.4", {"start": v(94, -24) * mm, "end": v(94, -27) * mm});
            skLineSegment(sketch, "E51.direction1", {"start": v(-16, -6) * mm, "end": v(94, -6) * mm, "construction": true});
            skLineSegment(sketch, "E51.direction2", {"start": v(-16, -6) * mm, "end": v(-16, -27) * mm, "construction": true});
            skLineSegment(sketch, "E52.bottom", {"start": v(108, -20) * mm, "end": v(105, -20) * mm});
            skLineSegment(sketch, "E52.top", {"start": v(108, -10) * mm, "end": v(105, -10) * mm});
            skLineSegment(sketch, "E52.left", {"start": v(108, -20) * mm, "end": v(108, -10) * mm});
            skLineSegment(sketch, "E52.right", {"start": v(105, -20) * mm, "end": v(105, -10) * mm});
            skPoint(sketch, "E52.middle", {"position": v(106.5, -15) * mm});
            skLineSegment(sketch, "E53.bottom", {"start": v(-17, -20) * mm, "end": v(-20, -20) * mm});
            skLineSegment(sketch, "E53.top", {"start": v(-17, -10) * mm, "end": v(-20, -10) * mm});
            skLineSegment(sketch, "E53.left", {"start": v(-17, -20) * mm, "end": v(-17, -10) * mm});
            skLineSegment(sketch, "E53.right", {"start": v(-20, -20) * mm, "end": v(-20, -10) * mm});
            skPoint(sketch, "E53.middle", {"position": v(-18.5, -15) * mm});
            skLineSegment(sketch, "E54", {"start": v(-45.57, -15) * mm, "end": v(123.66, -15) * mm, "construction": true});
            skPoint(sketch, "E54.startSnap0", {"position": v(-26, -15) * mm});
            skSolve(sketch);
        }
        {
            var Q0;
            Q0=makeQuery(id+"F7.imprint","IMPRINT",FACE,{"disambiguationData":[TD([[makeQuery(id+"F7.imprint","IMPRINT",EDGE,{"derivedFrom":sQuery(id+"F7.wireOp",EDGE,"E49.bottom")}),-1.0]])]});
            extrude(context, id + "F8", {"entities" : qUnion([Q0]), "oppositeDirection" : true, "depth" : getVariable(context, 'thickness')});
        }
        {
            var Q0;
            Q0=makeQuery(id+"F8.opExtrude","SWEPT_FACE",FACE,{"disambiguationData":[OSD([sQuery(id+"F7.wireOp",EDGE,"E49.right")])]});
            var sketch = newSketch(context, id + "F9", { "sketchPlane" : qUnion([Q0])});
            skLineSegment(sketch, "E55.0", {"start": v(-57, 0) * mm, "end": v(-57, -30) * mm});
            skLineSegment(sketch, "E56", {"start": v(-57, 0) * mm, "end": v(57, 0) * mm});
            skLineSegment(sketch, "E57", {"start": v(57, 0) * mm, "end": v(57, -30) * mm});
            skLineSegment(sketch, "E58", {"start": v(57, -30) * mm, "end": v(-57, -30) * mm});
            skCircle(sketch, "E59", {"center": v(-53, -15) * mm, "radius": 1.5 * mm});
            skPoint(sketch, "E59.centerSnap0", {"position": v(-57, -15) * mm});
            skCircle(sketch, "E60", {"center": v(53, -15) * mm, "radius": 1.5 * mm});
            skPoint(sketch, "E60.centerSnap0", {"position": v(57, -15) * mm});
            skSolve(sketch);
        }
        {
            var Q0;
            Q0=makeQuery(id+"F9.imprint","IMPRINT",FACE,{"disambiguationData":[TD([[makeQuery(id+"F9.imprint","IMPRINT",EDGE,{"derivedFrom":sQuery(id+"F9.wireOp",EDGE,"E55.0")}),1.0]])]});
            extrude(context, id + "F10", {"entities" : qUnion([Q0]), "oppositeDirection" : true, "depth" : 3 * mm});
        }
        {
            var Q0;
            Q0=makeQuery(id+"F8.opExtrude","SWEPT_FACE",FACE,{"disambiguationData":[OSD([sQuery(id+"F7.wireOp",EDGE,"E49.left")])]});
            var sketch = newSketch(context, id + "F11", { "sketchPlane" : qUnion([Q0])});
            skLineSegment(sketch, "E61.bottom", {"start": v(57, 0) * mm, "end": v(-57, 0) * mm});
            skLineSegment(sketch, "E61.top", {"start": v(57, -30) * mm, "end": v(-57, -30) * mm});
            skLineSegment(sketch, "E61.left", {"start": v(57, 0) * mm, "end": v(57, -30) * mm});
            skLineSegment(sketch, "E61.right", {"start": v(-57, 0) * mm, "end": v(-57, -30) * mm});
            skCircle(sketch, "E62", {"center": v(-53, -15) * mm, "radius": 1.5 * mm});
            skPoint(sketch, "E62.centerSnap0", {"position": v(-57, -15) * mm});
            skCircle(sketch, "E63", {"center": v(53, -15) * mm, "radius": 1.5 * mm});
            skPoint(sketch, "E63.centerSnap0", {"position": v(57, -15) * mm});
            skLineSegment(sketch, "E64.bottom", {"start": v(9, -14) * mm, "end": v(19.5, -14) * mm});
            skLineSegment(sketch, "E64.top", {"start": v(9, -27) * mm, "end": v(19.5, -27) * mm});
            skLineSegment(sketch, "E64.left", {"start": v(9, -14) * mm, "end": v(9, -27) * mm});
            skLineSegment(sketch, "E64.right", {"start": v(19.5, -14) * mm, "end": v(19.5, -27) * mm});
            skLineSegment(sketch, "E65", {"start": v(0, 0) * mm, "end": v(0, -30) * mm, "construction": true});
            skLineSegment(sketch, "E66.bottom", {"start": v(-21.45, -27) * mm, "end": v(-9.45, -27) * mm});
            skLineSegment(sketch, "E66.top", {"start": v(-21.45, -20) * mm, "end": v(-9.45, -20) * mm});
            skLineSegment(sketch, "E66.left", {"start": v(-21.45, -27) * mm, "end": v(-21.45, -20) * mm});
            skLineSegment(sketch, "E66.right", {"start": v(-9.45, -27) * mm, "end": v(-9.45, -20) * mm});
            skLineSegment(sketch, "E67.bottom", {"start": v(6.55, -20) * mm, "end": v(-5.45, -20) * mm});
            skLineSegment(sketch, "E67.top", {"start": v(6.55, -27) * mm, "end": v(-5.45, -27) * mm});
            skLineSegment(sketch, "E67.left", {"start": v(6.55, -20) * mm, "end": v(6.55, -27) * mm});
            skLineSegment(sketch, "E67.right", {"start": v(-5.45, -20) * mm, "end": v(-5.45, -27) * mm});
            skSolve(sketch);
        }
        {
            var Q0;
            Q0 = qSketchRegion(id + "F11", true);
            extrude(context, id + "F12", {"entities" : qUnion([Q0]), "oppositeDirection" : true, "depth" : 3 * mm});
        }
        {
            var Q0;
            Q0=makeQuery(id+"F12.opExtrude","SWEPT_FACE",FACE,{"disambiguationData":[OSD([sQuery(id+"F11.wireOp",EDGE,"E61.top")])]});
            var sketch = newSketch(context, id + "F13", { "sketchPlane" : qUnion([Q0])});
            skLineSegment(sketch, "E68.bottom", {"start": v(-60, -26) * mm, "end": v(60, -26) * mm});
            skLineSegment(sketch, "E68.top", {"start": v(-60, 114) * mm, "end": v(60, 114) * mm});
            skLineSegment(sketch, "E68.left", {"start": v(-60, -26) * mm, "end": v(-60, 114) * mm});
            skLineSegment(sketch, "E68.right", {"start": v(60, -26) * mm, "end": v(60, 114) * mm});
            skCircle(sketch, "E69", {"center": v(53, -11) * mm, "radius": 1.5 * mm});
            skCircle(sketch, "E70", {"center": v(-53, -11) * mm, "radius": 1.5 * mm});
            skCircle(sketch, "E71", {"center": v(-53, 99) * mm, "radius": 1.5 * mm});
            skCircle(sketch, "E72", {"center": v(53, 99) * mm, "radius": 1.5 * mm});
            skSolve(sketch);
        }
        {
            var Q0;
            Q0 = qSketchRegion(id + "F13", true);
            extrude(context, id + "F14", {"entities" : qUnion([Q0]), "depth" : getVariable(context, 'thickness')});
        }
        {
            var Q0;
            Q0=makeQuery(id+"F14.opExtrude","CAP_FACE",FACE,{"disambiguationData":[OSD([sQuery(id+"F13.wireOp",EDGE,"E68.bottom"),sQuery(id+"F13.wireOp",EDGE,"E68.top"),sQuery(id+"F13.wireOp",EDGE,"E68.left"),sQuery(id+"F13.wireOp",EDGE,"E68.right"),sQuery(id+"F13.wireOp",EDGE,"E69"),sQuery(id+"F13.wireOp",EDGE,"E70"),sQuery(id+"F13.wireOp",EDGE,"E71"),sQuery(id+"F13.wireOp",EDGE,"E72")])],"isStart":true});
            var sketch = newSketch(context, id + "F15", { "sketchPlane" : qUnion([Q0])});
            skLineSegment(sketch, "E73", {"start": v(-20, -111) * mm, "end": v(20, -111) * mm});
            skArc(sketch, "E74", {"start": v(20, -111) * mm, "mid": v(18.54, -107.46) * mm, "end": v(15, -106) * mm});
            skArc(sketch, "E75", {"start": v(-20, -111) * mm, "mid": v(-18.54, -107.46) * mm, "end": v(-15, -106) * mm});
            skLineSegment(sketch, "E76", {"start": v(-15, -106) * mm, "end": v(15, -106) * mm});
            skLineSegment(sketch, "E77", {"start": v(0, 46.25) * mm, "end": v(0, -160.2) * mm, "construction": true});
            skLineSegment(sketch, "E78", {"start": v(-88.34, -44) * mm, "end": v(100.62, -44) * mm, "construction": true});
            skPoint(sketch, "E78.startSnap0", {"position": v(-60, -44) * mm});
            skLineSegment(sketch, "E79", {"start": v(-57, -79) * mm, "end": v(-57, -9) * mm});
            skLineSegment(sketch, "E80", {"start": v(-52, -14) * mm, "end": v(-52, -74) * mm});
            skArc(sketch, "E81", {"start": v(-57, -79) * mm, "mid": v(-53.46, -77.54) * mm, "end": v(-52, -74) * mm});
            skArc(sketch, "E82", {"start": v(-57, -9) * mm, "mid": v(-53.46, -10.46) * mm, "end": v(-52, -14) * mm});
            skArc(sketch, "E83.MirrorCS", {"start": v(57, -79) * mm, "mid": v(53.46, -77.54) * mm, "end": v(52, -74) * mm});
            skLineSegment(sketch, "E84.MirrorCS", {"start": v(57, -79) * mm, "end": v(57, -9) * mm});
            skLineSegment(sketch, "E85.MirrorCS", {"start": v(52, -14) * mm, "end": v(52, -74) * mm});
            skArc(sketch, "E86.MirrorCS", {"start": v(57, -9) * mm, "mid": v(53.46, -10.46) * mm, "end": v(52, -14) * mm});
            skCircle(sketch, "E87.0", {"center": v(45.5, -54) * mm, "radius": 3.1 * mm, "construction": true});
            skCircle(sketch, "E87.1", {"center": v(-45.5, -54) * mm, "radius": 3.1 * mm, "construction": true});
            skLineSegment(sketch, "E88", {"start": v(45.5, -54) * mm, "end": v(-45.5, -54) * mm, "construction": true});
            skLineSegment(sketch, "E89.bottom", {"start": v(-5, -55.5) * mm, "end": v(5, -55.5) * mm});
            skLineSegment(sketch, "E89.top", {"start": v(-5, -52.5) * mm, "end": v(5, -52.5) * mm});
            skLineSegment(sketch, "E89.left", {"start": v(-5, -55.5) * mm, "end": v(-5, -52.5) * mm});
            skLineSegment(sketch, "E89.right", {"start": v(5, -55.5) * mm, "end": v(5, -52.5) * mm});
            skPoint(sketch, "E89.middle", {"position": v(0, -54) * mm});
            skLineSegment(sketch, "E90.bottom", {"start": v(-8, -58.5) * mm, "end": v(8, -58.5) * mm});
            skLineSegment(sketch, "E90.top", {"start": v(-8, -49.5) * mm, "end": v(8, -49.5) * mm});
            skLineSegment(sketch, "E90.left", {"start": v(-8, -58.5) * mm, "end": v(-8, -49.5) * mm});
            skLineSegment(sketch, "E90.right", {"start": v(8, -58.5) * mm, "end": v(8, -49.5) * mm});
            skSolve(sketch);
        }
        {
            var Q0;
            Q0 = qSketchRegion(id + "F15", true);
            extrude(context, id + "F16", {"entities" : qUnion([Q0]), "operationType" : NewBodyOperationType.ADD, "depth" : 3 * mm});
        }
        {
            var Q0;
            Q0=makeQuery(id+"F2.opExtrude","CAP_FACE",FACE,{"disambiguationData":[OSD([sQuery(id+"F1.wireOp",EDGE,"E0.bottom"),sQuery(id+"F1.wireOp",EDGE,"E0.top"),sQuery(id+"F1.wireOp",EDGE,"E0.left"),sQuery(id+"F1.wireOp",EDGE,"E0.right"),sQuery(id+"F1.wireOp",EDGE,"E1"),sQuery(id+"F1.wireOp",EDGE,"E2"),sQuery(id+"F1.wireOp",EDGE,"E4.bottom"),sQuery(id+"F1.wireOp",EDGE,"E4.top"),sQuery(id+"F1.wireOp",EDGE,"E4.left"),sQuery(id+"F1.wireOp",EDGE,"E4.right"),sQuery(id+"F1.wireOp",EDGE,"E5"),sQuery(id+"F1.wireOp",EDGE,"E6"),sQuery(id+"F1.wireOp",EDGE,"E8"),sQuery(id+"F1.wireOp",EDGE,"E9.bottom"),sQuery(id+"F1.wireOp",EDGE,"E9.top"),sQuery(id+"F1.wireOp",EDGE,"E9.left"),sQuery(id+"F1.wireOp",EDGE,"E9.right"),sQuery(id+"F1.wireOp",EDGE,"E10.1.0.0"),sQuery(id+"F1.wireOp",EDGE,"E10.1.0.2"),sQuery(id+"F1.wireOp",EDGE,"E10.1.0.3"),sQuery(id+"F1.wireOp",EDGE,"E10.1.0.4"),sQuery(id+"F1.wireOp",EDGE,"E10.1.0.5"),sQuery(id+"F1.wireOp",EDGE,"E10.2.0.0"),sQuery(id+"F1.wireOp",EDGE,"E10.2.0.2"),sQuery(id+"F1.wireOp",EDGE,"E10.2.0.3"),sQuery(id+"F1.wireOp",EDGE,"E10.2.0.4"),sQuery(id+"F1.wireOp",EDGE,"E10.2.0.5"),sQuery(id+"F1.wireOp",EDGE,"E10.3.0.0"),sQuery(id+"F1.wireOp",EDGE,"E10.3.0.2"),sQuery(id+"F1.wireOp",EDGE,"E10.3.0.3"),sQuery(id+"F1.wireOp",EDGE,"E10.3.0.4"),sQuery(id+"F1.wireOp",EDGE,"E10.3.0.5"),sQuery(id+"F1.wireOp",EDGE,"E10.4.0.0"),sQuery(id+"F1.wireOp",EDGE,"E10.4.0.2"),sQuery(id+"F1.wireOp",EDGE,"E10.4.0.3"),sQuery(id+"F1.wireOp",EDGE,"E10.4.0.4"),sQuery(id+"F1.wireOp",EDGE,"E10.4.0.5"),sQuery(id+"F1.wireOp",EDGE,"E10.5.0.0"),sQuery(id+"F1.wireOp",EDGE,"E10.5.0.2"),sQuery(id+"F1.wireOp",EDGE,"E10.5.0.3"),sQuery(id+"F1.wireOp",EDGE,"E10.5.0.4"),sQuery(id+"F1.wireOp",EDGE,"E10.5.0.5"),sQuery(id+"F1.wireOp",EDGE,"E10.6.0.0"),sQuery(id+"F1.wireOp",EDGE,"E10.6.0.2"),sQuery(id+"F1.wireOp",EDGE,"E10.6.0.3"),sQuery(id+"F1.wireOp",EDGE,"E10.6.0.4"),sQuery(id+"F1.wireOp",EDGE,"E10.6.0.5"),sQuery(id+"F1.wireOp",EDGE,"E10.7.0.0"),sQuery(id+"F1.wireOp",EDGE,"E10.7.0.2"),sQuery(id+"F1.wireOp",EDGE,"E10.7.0.3"),sQuery(id+"F1.wireOp",EDGE,"E10.7.0.4"),sQuery(id+"F1.wireOp",EDGE,"E10.7.0.5"),sQuery(id+"F1.wireOp",EDGE,"E11.1.0.0"),sQuery(id+"F1.wireOp",EDGE,"E11.1.0.3"),sQuery(id+"F1.wireOp",EDGE,"E11.1.0.4"),sQuery(id+"F1.wireOp",EDGE,"E11.1.0.6"),sQuery(id+"F1.wireOp",EDGE,"E11.1.0.7"),sQuery(id+"F1.wireOp",EDGE,"E11.1.0.8"),sQuery(id+"F1.wireOp",EDGE,"E11.1.0.9"),sQuery(id+"F1.wireOp",EDGE,"E11.1.0.10"),sQuery(id+"F1.wireOp",EDGE,"E11.1.0.11"),sQuery(id+"F1.wireOp",EDGE,"E11.1.0.12"),sQuery(id+"F1.wireOp",EDGE,"E11.1.0.13"),sQuery(id+"F1.wireOp",EDGE,"E11.1.0.14"),sQuery(id+"F1.wireOp",EDGE,"E11.1.0.15"),sQuery(id+"F1.wireOp",EDGE,"E11.1.0.16"),sQuery(id+"F1.wireOp",EDGE,"E11.1.0.17"),sQuery(id+"F1.wireOp",EDGE,"E12.1.0.1"),sQuery(id+"F1.wireOp",EDGE,"E12.1.0.2"),sQuery(id+"F1.wireOp",EDGE,"E12.1.0.3"),sQuery(id+"F1.wireOp",EDGE,"E12.1.0.4"),sQuery(id+"F1.wireOp",EDGE,"E12.1.0.5"),sQuery(id+"F1.wireOp",EDGE,"E13.1.2.0"),sQuery(id+"F1.wireOp",EDGE,"E13.3.2.0"),sQuery(id+"F1.wireOp",EDGE,"E13.6.2.0"),sQuery(id+"F1.wireOp",EDGE,"E13.9.2.0"),sQuery(id+"F1.wireOp",EDGE,"E13.12.2.0"),sQuery(id+"F1.wireOp",EDGE,"E14.1.0.0"),sQuery(id+"F1.wireOp",EDGE,"E14.1.0.1"),sQuery(id+"F1.wireOp",EDGE,"E14.1.0.2"),sQuery(id+"F1.wireOp",EDGE,"E14.1.0.3"),sQuery(id+"F1.wireOp",EDGE,"E14.1.0.5"),sQuery(id+"F1.wireOp",EDGE,"E14.2.0.0"),sQuery(id+"F1.wireOp",EDGE,"E14.2.0.1"),sQuery(id+"F1.wireOp",EDGE,"E14.2.0.2"),sQuery(id+"F1.wireOp",EDGE,"E14.2.0.3"),sQuery(id+"F1.wireOp",EDGE,"E14.2.0.5"),sQuery(id+"F1.wireOp",EDGE,"E14.3.0.0"),sQuery(id+"F1.wireOp",EDGE,"E14.3.0.1"),sQuery(id+"F1.wireOp",EDGE,"E14.3.0.2"),sQuery(id+"F1.wireOp",EDGE,"E14.3.0.3"),sQuery(id+"F1.wireOp",EDGE,"E14.3.0.5"),sQuery(id+"F1.wireOp",EDGE,"E14.4.0.0"),sQuery(id+"F1.wireOp",EDGE,"E14.4.0.1"),sQuery(id+"F1.wireOp",EDGE,"E14.4.0.2"),sQuery(id+"F1.wireOp",EDGE,"E14.4.0.3"),sQuery(id+"F1.wireOp",EDGE,"E14.4.0.5"),sQuery(id+"F1.wireOp",EDGE,"E14.5.0.0"),sQuery(id+"F1.wireOp",EDGE,"E14.5.0.1"),sQuery(id+"F1.wireOp",EDGE,"E14.5.0.2"),sQuery(id+"F1.wireOp",EDGE,"E14.5.0.3"),sQuery(id+"F1.wireOp",EDGE,"E14.5.0.5"),sQuery(id+"F1.wireOp",EDGE,"E14.6.0.0"),sQuery(id+"F1.wireOp",EDGE,"E14.6.0.1"),sQuery(id+"F1.wireOp",EDGE,"E14.6.0.2"),sQuery(id+"F1.wireOp",EDGE,"E14.6.0.3"),sQuery(id+"F1.wireOp",EDGE,"E14.6.0.5"),sQuery(id+"F1.wireOp",EDGE,"E14.7.0.0"),sQuery(id+"F1.wireOp",EDGE,"E14.7.0.1"),sQuery(id+"F1.wireOp",EDGE,"E14.7.0.2"),sQuery(id+"F1.wireOp",EDGE,"E14.7.0.3"),sQuery(id+"F1.wireOp",EDGE,"E14.7.0.5"),sQuery(id+"F1.wireOp",EDGE,"E15"),sQuery(id+"F1.wireOp",EDGE,"E16"),sQuery(id+"F1.wireOp",EDGE,"E17"),sQuery(id+"F1.wireOp",EDGE,"E18")])],"isStart":true});
            var sketch = newSketch(context, id + "F17", { "sketchPlane" : qUnion([Q0])});
            skLineSegment(sketch, "E91", {"start": v(0, -27.81) * mm, "end": v(0, 118.1) * mm, "construction": true});
            skLineSegment(sketch, "E92.bottom", {"start": v(5, 52.5) * mm, "end": v(-5, 52.5) * mm});
            skLineSegment(sketch, "E92.top", {"start": v(5, 55.5) * mm, "end": v(-5, 55.5) * mm});
            skLineSegment(sketch, "E92.left", {"start": v(5, 52.5) * mm, "end": v(5, 55.5) * mm});
            skLineSegment(sketch, "E92.right", {"start": v(-5, 52.5) * mm, "end": v(-5, 55.5) * mm});
            skLineSegment(sketch, "E93.bottom", {"start": v(8, 49.5) * mm, "end": v(-8, 49.5) * mm});
            skLineSegment(sketch, "E93.top", {"start": v(8, 58.5) * mm, "end": v(-8, 58.5) * mm});
            skLineSegment(sketch, "E93.left", {"start": v(8, 49.5) * mm, "end": v(8, 58.5) * mm});
            skLineSegment(sketch, "E93.right", {"start": v(-8, 49.5) * mm, "end": v(-8, 58.5) * mm});
            skLineSegment(sketch, "E94", {"start": v(45.5, 54) * mm, "end": v(-45.5, 54) * mm, "construction": true});
            skLineSegment(sketch, "E95", {"start": v(20, 111) * mm, "end": v(-20, 111) * mm});
            skLineSegment(sketch, "E96", {"start": v(15, 106) * mm, "end": v(-15, 106) * mm});
            skArc(sketch, "E97", {"start": v(20, 111) * mm, "mid": v(18.54, 107.46) * mm, "end": v(15, 106) * mm});
            skArc(sketch, "E98", {"start": v(-20, 111) * mm, "mid": v(-18.54, 107.46) * mm, "end": v(-15, 106) * mm});
            skLineSegment(sketch, "E99", {"start": v(-57, 79) * mm, "end": v(-57, 9) * mm});
            skLineSegment(sketch, "E100", {"start": v(-52, 74) * mm, "end": v(-52, 14) * mm});
            skArc(sketch, "E101", {"start": v(-57, 9) * mm, "mid": v(-53.46, 10.46) * mm, "end": v(-52, 14) * mm});
            skArc(sketch, "E102", {"start": v(-57, 79) * mm, "mid": v(-53.46, 77.54) * mm, "end": v(-52, 74) * mm});
            skLineSegment(sketch, "E103", {"start": v(74.52, 44) * mm, "end": v(-78.2, 44) * mm, "construction": true});
            skPoint(sketch, "E103.startSnap0", {"position": v(60, 44) * mm});
            skLineSegment(sketch, "E104.MirrorCS", {"start": v(52, 74) * mm, "end": v(52, 14) * mm});
            skLineSegment(sketch, "E105.MirrorCS", {"start": v(57, 79) * mm, "end": v(57, 9) * mm});
            skArc(sketch, "E106.MirrorCS", {"start": v(57, 79) * mm, "mid": v(53.46, 77.54) * mm, "end": v(52, 74) * mm});
            skArc(sketch, "E107.MirrorCS", {"start": v(57, 9) * mm, "mid": v(53.46, 10.46) * mm, "end": v(52, 14) * mm});
            skArc(sketch, "E108.MirrorCS", {"start": v(-20, -23) * mm, "mid": v(-18.54, -19.46) * mm, "end": v(-15, -18) * mm});
            skLineSegment(sketch, "E109.MirrorCS", {"start": v(15, -18) * mm, "end": v(-15, -18) * mm});
            skLineSegment(sketch, "E110.MirrorCS", {"start": v(20, -23) * mm, "end": v(-20, -23) * mm});
            skArc(sketch, "E111.MirrorCS", {"start": v(20, -23) * mm, "mid": v(18.54, -19.46) * mm, "end": v(15, -18) * mm});
            skSolve(sketch);
        }
        {
            var Q0;
            Q0=makeQuery(id+"F17.imprint","IMPRINT",FACE,{"disambiguationData":[TD([[makeQuery(id+"F17.imprint","IMPRINT",EDGE,{"derivedFrom":sQuery(id+"F17.wireOp",EDGE,"E95")}),1.0]])]});
            var Q1;
            Q1=makeQuery(id+"F17.imprint","IMPRINT",FACE,{"disambiguationData":[TD([[makeQuery(id+"F17.imprint","IMPRINT",EDGE,{"derivedFrom":sQuery(id+"F17.wireOp",EDGE,"E92.bottom")}),1.0]])]});
            var Q2;
            Q2=makeQuery(id+"F17.imprint","IMPRINT",FACE,{"disambiguationData":[TD([[makeQuery(id+"F17.imprint","IMPRINT",EDGE,{"derivedFrom":sQuery(id+"F17.wireOp",EDGE,"E99")}),1.0]])]});
            var Q3;
            Q3=makeQuery(id+"F17.imprint","IMPRINT",FACE,{"disambiguationData":[TD([[makeQuery(id+"F17.imprint","IMPRINT",EDGE,{"derivedFrom":sQuery(id+"F17.wireOp",EDGE,"E104.MirrorCS")}),1.0]])]});
            var Q4;
            Q4=makeQuery(id+"F17.imprint","IMPRINT",FACE,{"disambiguationData":[TD([[makeQuery(id+"F17.imprint","IMPRINT",EDGE,{"derivedFrom":sQuery(id+"F17.wireOp",EDGE,"E108.MirrorCS")}),-1.0]])]});
            extrude(context, id + "F18", {"entities" : qUnion([Q0, Q1, Q2, Q3, Q4]), "operationType" : NewBodyOperationType.ADD, "depth" : getVariable(context, 'thickness')});
        }
        {
            var Q0;
            Q0=makeQuery(id+"F18.opExtrude","SWEPT_FACE",FACE,{"disambiguationData":[OSD([sQuery(id+"F17.wireOp",EDGE,"E92.top")])]});
            var sketch = newSketch(context, id + "F19", { "sketchPlane" : qUnion([Q0])});
            skLineSegment(sketch, "E112.0", {"start": v(5, -3) * mm, "end": v(5, 0) * mm});
            skLineSegment(sketch, "E112.1", {"start": v(-5, 0) * mm, "end": v(5, 0) * mm});
            skLineSegment(sketch, "E112.2", {"start": v(-5, -3) * mm, "end": v(-5, 0) * mm});
            skLineSegment(sketch, "E113", {"start": v(5, -3) * mm, "end": v(8, -3) * mm});
            skLineSegment(sketch, "E114", {"start": v(8, -3) * mm, "end": v(8, -27) * mm});
            skLineSegment(sketch, "E115", {"start": v(8, -27) * mm, "end": v(5, -27) * mm});
            skLineSegment(sketch, "E116", {"start": v(5, -27) * mm, "end": v(5, -30) * mm});
            skLineSegment(sketch, "E117", {"start": v(5, -30) * mm, "end": v(-5, -30) * mm});
            skLineSegment(sketch, "E118", {"start": v(-5, -30) * mm, "end": v(-5, -27) * mm});
            skLineSegment(sketch, "E119", {"start": v(-5, -27) * mm, "end": v(-8, -27) * mm});
            skLineSegment(sketch, "E120", {"start": v(-8, -27) * mm, "end": v(-8, -3) * mm});
            skLineSegment(sketch, "E121", {"start": v(-8, -3) * mm, "end": v(-5, -3) * mm});
            skSolve(sketch);
        }
        {
            var Q0;
            Q0 = qSketchRegion(id + "F19", true);
            extrude(context, id + "F20", {"entities" : qUnion([Q0]), "depth" : getVariable(context, 'thickness')});
        }
        {
            var Q0;
            Q0=makeQuery(id+"F14.opExtrude","CAP_FACE",FACE,{"disambiguationData":[OSD([sQuery(id+"F13.wireOp",EDGE,"E68.bottom"),sQuery(id+"F13.wireOp",EDGE,"E68.top"),sQuery(id+"F13.wireOp",EDGE,"E68.left"),sQuery(id+"F13.wireOp",EDGE,"E68.right"),sQuery(id+"F13.wireOp",EDGE,"E69"),sQuery(id+"F13.wireOp",EDGE,"E70"),sQuery(id+"F13.wireOp",EDGE,"E71"),sQuery(id+"F13.wireOp",EDGE,"E72")])],"isStart":false});
            var sketch = newSketch(context, id + "F21", { "sketchPlane" : qUnion([Q0])});
            skLineSegment(sketch, "E122", {"start": v(0, -41.34) * mm, "end": v(0, 137.52) * mm, "construction": true});
            skPoint(sketch, "E122.startSnap0", {"position": v(0, -26) * mm});
            skLineSegment(sketch, "E123", {"start": v(80.04, 44) * mm, "end": v(-86.74, 44) * mm, "construction": true});
            skPoint(sketch, "E123.startSnap0", {"position": v(60, 44) * mm});
            skLineSegment(sketch, "E124", {"start": v(14.35, 54) * mm, "end": v(-14.32, 54) * mm, "construction": true});
            skCircle(sketch, "E125", {"center": v(0, 54) * mm, "radius": 4 * mm});
            skCircle(sketch, "E126", {"center": v(52, 106) * mm, "radius": 4 * mm});
            skCircle(sketch, "E127", {"center": v(-52, 106) * mm, "radius": 4 * mm});
            skCircle(sketch, "E128", {"center": v(-52, -18) * mm, "radius": 4 * mm});
            skCircle(sketch, "E129", {"center": v(52, -18) * mm, "radius": 4 * mm});
            skSolve(sketch);
        }
        {
            var Q0;
            Q0 = qSketchRegion(id + "F21", true);
            extrude(context, id + "F22", {"entities" : qUnion([Q0]), "operationType" : NewBodyOperationType.REMOVE, "oppositeDirection" : true, "depth" : 0.1 * mm});
        }
        {
            var Q0;
            {var subQ0=sQuery(id+"F13.wireOp",EDGE,"E68.top");var subQ1=sQuery(id+"F13.wireOp",EDGE,"E68.right");var subQ2=sQuery(id+"F13.wireOp",EDGE,"E72");var subQ3=sQuery(id+"F13.wireOp",EDGE,"E68.left");var subQ4=sQuery(id+"F13.wireOp",EDGE,"E71");var subQ5=sQuery(id+"F13.wireOp",EDGE,"E68.bottom");var subQ6=sQuery(id+"F13.wireOp",EDGE,"E69");var subQ7=sQuery(id+"F13.wireOp",EDGE,"E70");Q0=makeQuery(id+"F16.boolean.opBoolean","SPLIT",FACE,{"disambiguationData":[TD([makeQuery(id+"F14.opExtrude","SWEPT_FACE",FACE,{"disambiguationData":[OSD([subQ5])]})])],"derivedFrom":makeQuery(id+"F14.opExtrude","CAP_FACE",FACE,{"disambiguationData":[OSD([subQ5,subQ0,subQ3,subQ1,subQ6,subQ7,subQ4,subQ2])],"isStart":true})});}
            var sketch = newSketch(context, id + "F23", { "sketchPlane" : qUnion([Q0])});
            skLineSegment(sketch, "E130", {"start": v(-21.95, 22.5) * mm, "end": v(-21.95, -43.6) * mm});
            skLineSegment(sketch, "E131", {"start": v(-19.05, -43.6) * mm, "end": v(-16.55, -46.1) * mm});
            skLineSegment(sketch, "E132", {"start": v(-16.55, -46.1) * mm, "end": v(15.75, -46.1) * mm});
            skLineSegment(sketch, "E133", {"start": v(15.75, -46.1) * mm, "end": v(18.25, -43.6) * mm});
            skLineSegment(sketch, "E134", {"start": v(18.25, -43.6) * mm, "end": v(28.85, -43.6) * mm});
            skLineSegment(sketch, "E135", {"start": v(28.85, -43.6) * mm, "end": v(31.35, -41.1) * mm});
            skLineSegment(sketch, "E136", {"start": v(31.35, -41.1) * mm, "end": v(31.35, 22.5) * mm});
            skLineSegment(sketch, "E137", {"start": v(31.35, 22.5) * mm, "end": v(-21.95, 22.5) * mm});
            skLineSegment(sketch, "E138", {"start": v(-21.95, -43.6) * mm, "end": v(-19.05, -43.6) * mm});
            skCircle(sketch, "E139", {"center": v(-19.45, 8.5) * mm, "radius": 1.5 * mm});
            skCircle(sketch, "E140", {"center": v(28.75, 7.2) * mm, "radius": 1.5 * mm});
            skCircle(sketch, "E141", {"center": v(-14.35, -43.6) * mm, "radius": 1.5 * mm});
            skCircle(sketch, "E142", {"center": v(13.55, -43.6) * mm, "radius": 1.5 * mm});
            skLineSegment(sketch, "E143", {"start": v(-0.4, -42.5) * mm, "end": v(-0.4, -48) * mm, "construction": true});
            skSolve(sketch);
        }
        {
            var Q0;
            Q0=makeQuery(id+"F23.imprint","IMPRINT",FACE,{"disambiguationData":[TD([[makeQuery(id+"F23.imprint","IMPRINT",EDGE,{"derivedFrom":sQuery(id+"F23.wireOp",EDGE,"E139")}),1.0]])]});
            var Q1;
            Q1=makeQuery(id+"F23.imprint","IMPRINT",FACE,{"disambiguationData":[TD([[makeQuery(id+"F23.imprint","IMPRINT",EDGE,{"derivedFrom":sQuery(id+"F23.wireOp",EDGE,"E140")}),1.0]])]});
            var Q2;
            Q2=makeQuery(id+"F23.imprint","IMPRINT",FACE,{"disambiguationData":[TD([[makeQuery(id+"F23.imprint","IMPRINT",EDGE,{"derivedFrom":sQuery(id+"F23.wireOp",EDGE,"E142")}),1.0]])]});
            var Q3;
            Q3=makeQuery(id+"F23.imprint","IMPRINT",FACE,{"disambiguationData":[TD([[makeQuery(id+"F23.imprint","IMPRINT",EDGE,{"derivedFrom":sQuery(id+"F23.wireOp",EDGE,"E141")}),1.0]])]});
            extrude(context, id + "F24", {"entities" : qUnion([Q0, Q1, Q2, Q3]), "operationType" : NewBodyOperationType.REMOVE, "endBound" : BoundingType.THROUGH_ALL, "oppositeDirection" : true, "depth" : 25 * mm});
        }
        {
            var Q0;
            Q0=makeQuery(id+"F23.imprint","IMPRINT",FACE,{"disambiguationData":[TD([[makeQuery(id+"F23.imprint","IMPRINT",EDGE,{"derivedFrom":sQuery(id+"F23.wireOp",EDGE,"E130")}),1.0]])]});
            extrude(context, id + "F25", {"entities" : qUnion([Q0]), "depth" : 14 * mm});
        }
    });
